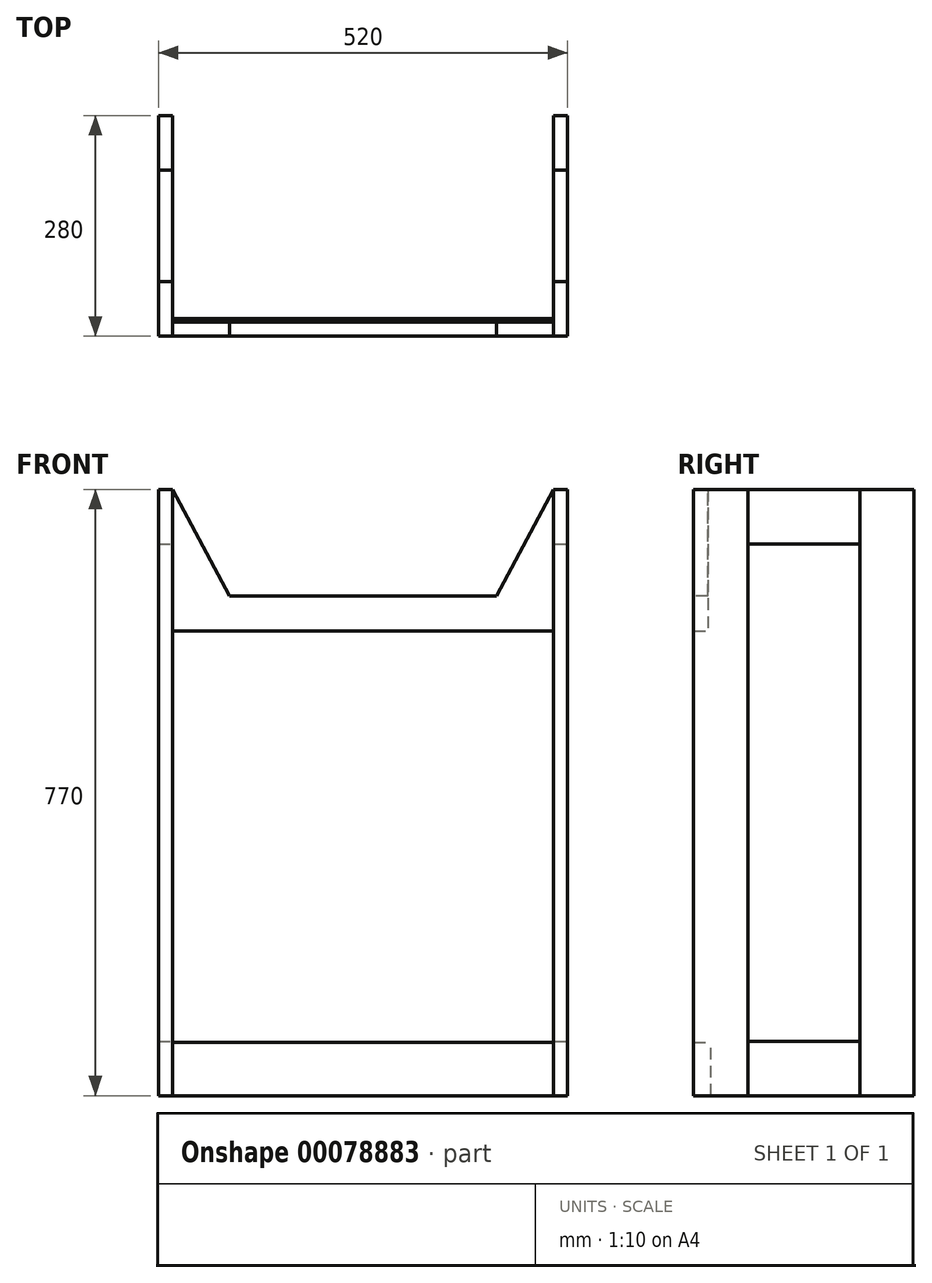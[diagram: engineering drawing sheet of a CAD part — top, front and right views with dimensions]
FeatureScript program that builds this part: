
annotation { "Feature Type Name" : "Feature", "Feature Type Description" : "" }
export const myFeature = defineFeature(function(context is Context, id is Id, definition is map)
    precondition{}
    {
        {
            var Q0;
            Q0=qCreatedBy(makeId("Top.planeOp"),FACE);
            var sketch = newSketch(context, id + "F0", { "sketchPlane" : qUnion([Q0])});
            skLineSegment(sketch, "E0.bottom", {"start": v(97.57, -67.85) * mm, "end": v(115.57, -67.85) * mm});
            skLineSegment(sketch, "E0.top", {"start": v(97.57, 1.15) * mm, "end": v(115.57, 1.15) * mm});
            skLineSegment(sketch, "E0.left", {"start": v(97.57, -67.85) * mm, "end": v(97.57, 1.15) * mm});
            skLineSegment(sketch, "E0.right", {"start": v(115.57, -67.85) * mm, "end": v(115.57, 1.15) * mm});
            skSolve(sketch);
        }
        {
            var Q0;
            Q0=makeQuery(id+"F0.imprint","IMPRINT",FACE,{"disambiguationData":[TD([[makeQuery(id+"F0.imprint","IMPRINT",EDGE,{"derivedFrom":sQuery(id+"F0.wireOp",EDGE,"E0.bottom")}),1.0]])]});
            extrude(context, id + "F1", {"entities" : qUnion([Q0]), "depth" : 770 * mm});
        }
        {
            var Q0;
            Q0=makeQuery(id+"F1.opExtrude","SWEPT_BODY",BODY,{"disambiguationData":[OSD([sQuery(id+"F0.wireOp",EDGE,"E0.bottom"),sQuery(id+"F0.wireOp",EDGE,"E0.top"),sQuery(id+"F0.wireOp",EDGE,"E0.left"),sQuery(id+"F0.wireOp",EDGE,"E0.right")])]});
            transform(context, id + "F2", {"entities" : qUnion([Q0]), "transformType" : TransformType.TRANSLATION_3D, "dx" : -502 * mm, "dy" : 211 * mm, "dz" : 0 * mm, "makeCopy" : true});
        }
        {
            var Q0;
            Q0=makeQuery(id+"F1.opExtrude","SWEPT_BODY",BODY,{"disambiguationData":[OSD([sQuery(id+"F0.wireOp",EDGE,"E0.bottom"),sQuery(id+"F0.wireOp",EDGE,"E0.top"),sQuery(id+"F0.wireOp",EDGE,"E0.left"),sQuery(id+"F0.wireOp",EDGE,"E0.right")])]});
            transform(context, id + "F3", {"entities" : qUnion([Q0]), "transformType" : TransformType.TRANSLATION_3D, "dx" : -502 * mm, "dy" : 0 * mm, "dz" : 0 * mm, "makeCopy" : true});
        }
        {
            var Q0;
            Q0=makeQuery(id+"F1.opExtrude","SWEPT_BODY",BODY,{"disambiguationData":[OSD([sQuery(id+"F0.wireOp",EDGE,"E0.bottom"),sQuery(id+"F0.wireOp",EDGE,"E0.top"),sQuery(id+"F0.wireOp",EDGE,"E0.left"),sQuery(id+"F0.wireOp",EDGE,"E0.right")])]});
            transform(context, id + "F4", {"entities" : qUnion([Q0]), "transformType" : TransformType.TRANSLATION_3D, "dx" : 0 * mm, "dy" : 211 * mm, "dz" : 0 * mm, "makeCopy" : true});
        }
        {
            var Q0;
            Q0=makeQuery(id+"F1.opExtrude","SWEPT_FACE",FACE,{"disambiguationData":[OSD([sQuery(id+"F0.wireOp",EDGE,"E0.top")])]});
            var sketch = newSketch(context, id + "F5", { "sketchPlane" : qUnion([Q0])});
            skLineSegment(sketch, "E1.bottom", {"start": v(-97.57, 770) * mm, "end": v(-115.57, 770) * mm});
            skLineSegment(sketch, "E1.top", {"start": v(-97.57, 701) * mm, "end": v(-115.57, 701) * mm});
            skLineSegment(sketch, "E1.left", {"start": v(-97.57, 770) * mm, "end": v(-97.57, 701) * mm});
            skLineSegment(sketch, "E1.right", {"start": v(-115.57, 770) * mm, "end": v(-115.57, 701) * mm});
            skSolve(sketch);
        }
        {
            var Q0;
            Q0=makeQuery(id+"F5.imprint","IMPRINT",FACE,{"disambiguationData":[TD([[makeQuery(id+"F5.imprint","IMPRINT",EDGE,{"derivedFrom":sQuery(id+"F5.wireOp",EDGE,"E1.bottom")}),1.0]])]});
            var Q1;
            Q1=makeQuery(id+"F4.opPattern","COPY",FACE,{"derivedFrom":makeQuery(id+"F1.opExtrude","SWEPT_FACE",FACE,{"disambiguationData":[OSD([sQuery(id+"F0.wireOp",EDGE,"E0.bottom")])]}),"instanceName":"1"});
            extrude(context, id + "F6", {"entities" : qUnion([Q0]), "endBound" : BoundingType.UP_TO_SURFACE, "endBoundEntityFace" : qUnion([Q1]), "depth" : 25 * mm});
        }
        {
            var Q0;
            Q0=makeQuery(id+"F6.opExtrude","SWEPT_BODY",BODY,{"disambiguationData":[OSD([sQuery(id+"F5.wireOp",EDGE,"E1.bottom"),sQuery(id+"F5.wireOp",EDGE,"E1.top"),sQuery(id+"F5.wireOp",EDGE,"E1.left"),sQuery(id+"F5.wireOp",EDGE,"E1.right")])]});
            transform(context, id + "F7", {"entities" : qUnion([Q0]), "transformType" : TransformType.TRANSLATION_3D, "dx" : 0 * mm, "dy" : 0 * mm, "dz" : -701 * mm, "makeCopy" : true});
        }
        {
            var Q0;
            Q0=makeQuery(id+"F6.opExtrude","SWEPT_BODY",BODY,{"disambiguationData":[OSD([sQuery(id+"F5.wireOp",EDGE,"E1.bottom"),sQuery(id+"F5.wireOp",EDGE,"E1.top"),sQuery(id+"F5.wireOp",EDGE,"E1.left"),sQuery(id+"F5.wireOp",EDGE,"E1.right")])]});
            transform(context, id + "F8", {"entities" : qUnion([Q0]), "transformType" : TransformType.TRANSLATION_3D, "dx" : -502 * mm, "dy" : 0 * mm, "dz" : 0 * mm, "makeCopy" : true});
        }
        {
            var Q0;
            Q0=makeQuery(id+"F6.opExtrude","SWEPT_BODY",BODY,{"disambiguationData":[OSD([sQuery(id+"F5.wireOp",EDGE,"E1.bottom"),sQuery(id+"F5.wireOp",EDGE,"E1.top"),sQuery(id+"F5.wireOp",EDGE,"E1.left"),sQuery(id+"F5.wireOp",EDGE,"E1.right")])]});
            transform(context, id + "F9", {"entities" : qUnion([Q0]), "transformType" : TransformType.TRANSLATION_3D, "dx" : -502 * mm, "dy" : 0 * mm, "dz" : -701 * mm, "makeCopy" : true});
        }
        {
            var Q0;
            Q0=makeQuery(id+"F1.opExtrude","SWEPT_FACE",FACE,{"disambiguationData":[OSD([sQuery(id+"F0.wireOp",EDGE,"E0.left")])]});
            var sketch = newSketch(context, id + "F10", { "sketchPlane" : qUnion([Q0])});
            skPoint(sketch, "E2.oppositeSnap0", {"position": v(49.85, 770) * mm});
            skLineSegment(sketch, "E2.bottom", {"start": v(67.85, 770) * mm, "end": v(49.85, 770) * mm});
            skLineSegment(sketch, "E2.top", {"start": v(67.85, 590) * mm, "end": v(49.85, 590) * mm});
            skLineSegment(sketch, "E2.left", {"start": v(67.85, 770) * mm, "end": v(67.85, 590) * mm});
            skLineSegment(sketch, "E2.right", {"start": v(49.85, 770) * mm, "end": v(49.85, 590) * mm});
            skSolve(sketch);
        }
        {
            var Q0;
            Q0=makeQuery(id+"F10.imprint","IMPRINT",FACE,{"disambiguationData":[TD([[makeQuery(id+"F10.imprint","IMPRINT",EDGE,{"derivedFrom":sQuery(id+"F10.wireOp",EDGE,"E2.bottom")}),1.0]])]});
            var Q1;
            Q1=makeQuery(id+"F3.opPattern","COPY",FACE,{"derivedFrom":makeQuery(id+"F1.opExtrude","SWEPT_FACE",FACE,{"disambiguationData":[OSD([sQuery(id+"F0.wireOp",EDGE,"E0.right")])]}),"instanceName":"1"});
            extrude(context, id + "F11", {"entities" : qUnion([Q0]), "endBound" : BoundingType.UP_TO_SURFACE, "endBoundEntityFace" : qUnion([Q1]), "depth" : 25 * mm});
        }
        {
            var Q0;
            Q0=makeQuery(id+"F11.opExtrude","SWEPT_FACE",FACE,{"disambiguationData":[OSD([sQuery(id+"F10.wireOp",EDGE,"E2.left")])]});
            var sketch = newSketch(context, id + "F12", { "sketchPlane" : qUnion([Q0])});
            skLineSegment(sketch, "E3", {"start": v(-144.43, 770) * mm, "end": v(-144.43, 635) * mm});
            skPoint(sketch, "E3.endSnap0", {"position": v(-144.43, 770) * mm});
            skLineSegment(sketch, "E4", {"start": v(-386.43, 770) * mm, "end": v(-314.1, 635) * mm});
            skLineSegment(sketch, "E5", {"start": v(97.57, 770) * mm, "end": v(25.24, 635) * mm});
            skLineSegment(sketch, "E6", {"start": v(25.24, 635) * mm, "end": v(-144.43, 635) * mm});
            skLineSegment(sketch, "E7", {"start": v(-314.1, 635) * mm, "end": v(-144.43, 635) * mm});
            skSolve(sketch);
        }
        {
            var Q0;
            {var subQ0=sQuery(id+"F12.wireOp",EDGE,"E3");Q0=makeQuery(id+"F12.imprint","IMPRINT",FACE,{"disambiguationData":[TD([[makeQuery(id+"F12.imprint","IMPRINT",EDGE,{"derivedFrom":subQ0}),-1.0]])]});}
            var Q1;
            {var subQ0=sQuery(id+"F12.wireOp",EDGE,"E3");Q1=makeQuery(id+"F12.imprint","IMPRINT",FACE,{"disambiguationData":[TD([[makeQuery(id+"F12.imprint","IMPRINT",EDGE,{"derivedFrom":subQ0}),1.0]])]});}
            extrude(context, id + "F13", {"entities" : qUnion([Q0, Q1]), "operationType" : NewBodyOperationType.REMOVE, "endBound" : BoundingType.UP_TO_NEXT, "oppositeDirection" : true, "depth" : 25 * mm});
        }
        {
            var Q0;
            Q0=makeQuery(id+"F1.opExtrude","SWEPT_FACE",FACE,{"disambiguationData":[OSD([sQuery(id+"F0.wireOp",EDGE,"E0.left")])]});
            var sketch = newSketch(context, id + "F14", { "sketchPlane" : qUnion([Q0])});
            skLineSegment(sketch, "E8.bottom", {"start": v(67.85, 0) * mm, "end": v(45.64, 0) * mm});
            skLineSegment(sketch, "E8.top", {"start": v(67.85, 67.51) * mm, "end": v(45.64, 67.51) * mm});
            skLineSegment(sketch, "E8.left", {"start": v(67.85, 0) * mm, "end": v(67.85, 67.51) * mm});
            skLineSegment(sketch, "E8.right", {"start": v(45.64, 0) * mm, "end": v(45.64, 67.51) * mm});
            skSolve(sketch);
        }
        {
            var Q0;
            Q0=makeQuery(id+"F14.imprint","IMPRINT",FACE,{"disambiguationData":[TD([[makeQuery(id+"F14.imprint","IMPRINT",EDGE,{"derivedFrom":sQuery(id+"F14.wireOp",EDGE,"E8.bottom")}),-1.0]])]});
            var Q1;
            Q1=makeQuery(id+"F3.opPattern","COPY",FACE,{"derivedFrom":makeQuery(id+"F1.opExtrude","SWEPT_FACE",FACE,{"disambiguationData":[OSD([sQuery(id+"F0.wireOp",EDGE,"E0.right")])]}),"instanceName":"1"});
            extrude(context, id + "F15", {"entities" : qUnion([Q0]), "endBound" : BoundingType.UP_TO_SURFACE, "endBoundEntityFace" : qUnion([Q1]), "depth" : 25 * mm});
        }
    });
